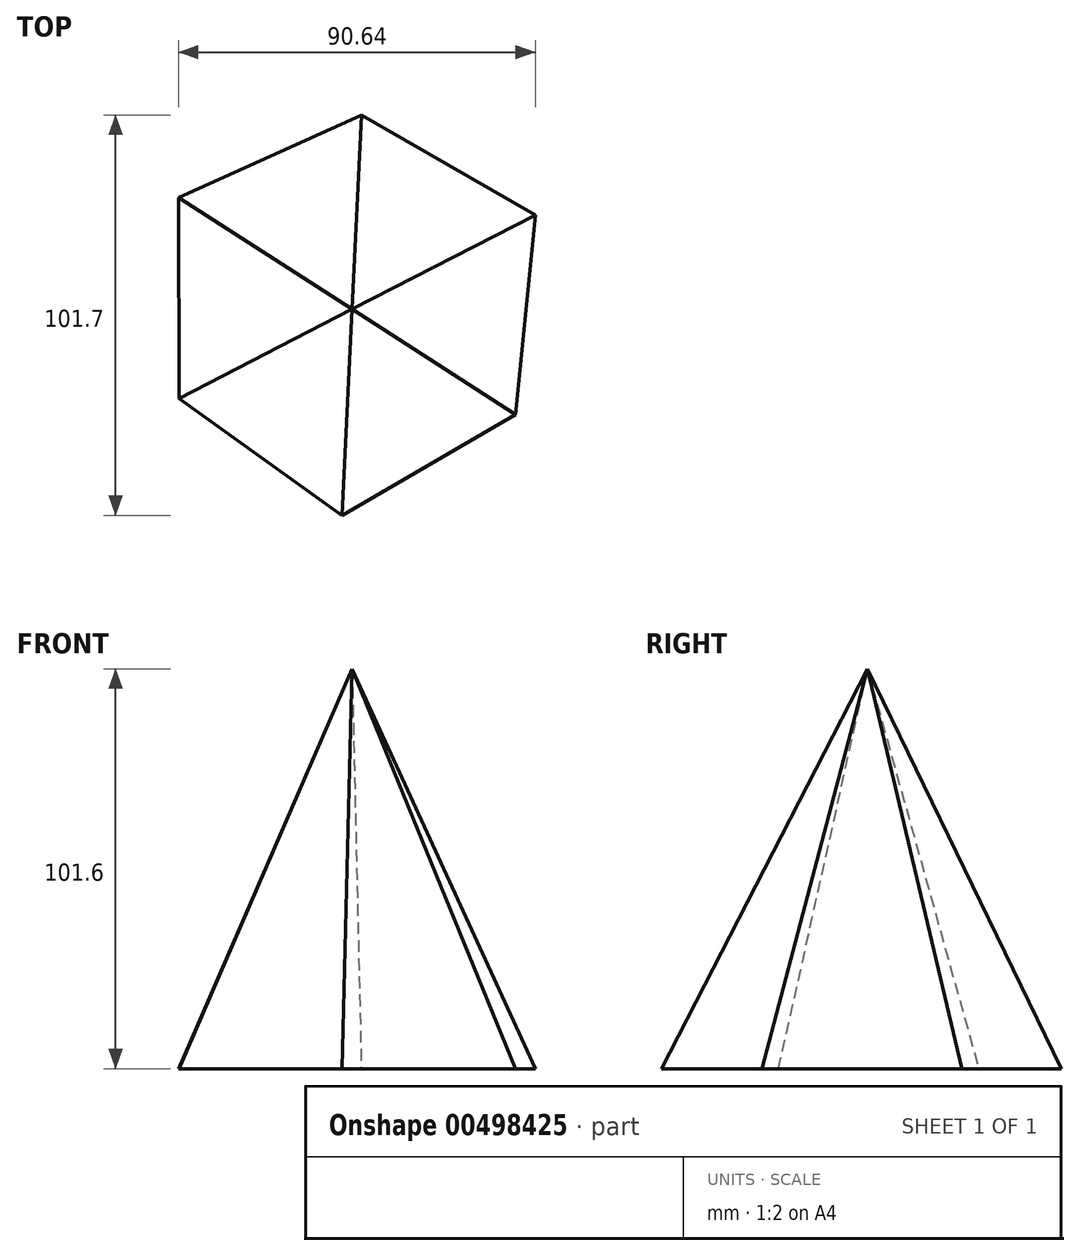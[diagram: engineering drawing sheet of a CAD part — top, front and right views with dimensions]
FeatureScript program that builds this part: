
annotation { "Feature Type Name" : "Feature", "Feature Type Description" : "" }
export const myFeature = defineFeature(function(context is Context, id is Id, definition is map)
    precondition{}
    {
        {
            var Q0;
            Q0=qCreatedBy(makeId("Top.planeOp"),FACE);
            var sketch = newSketch(context, id + "F0", { "sketchPlane" : qUnion([Q0])});
            skCircle(sketch, "E0.cCircle", {"center": v(0, 0) * mm, "radius": 87.99 * mm, "construction": true});
            skLineSegment(sketch, "E0.0", {"start": v(-44.2, 76.08) * mm, "end": v(87.99, 0.23) * mm});
            skLineSegment(sketch, "E0.1", {"start": v(87.99, 0.23) * mm, "end": v(-43.8, -76.32) * mm});
            skLineSegment(sketch, "E0.2", {"start": v(-43.8, -76.32) * mm, "end": v(-44.2, 76.08) * mm});
            skLineSegment(sketch, "E1.0", {"start": v(51.24, 71.53) * mm, "end": v(36.32, -80.14) * mm});
            skLineSegment(sketch, "E1.1", {"start": v(36.32, -80.14) * mm, "end": v(-87.57, 8.61) * mm});
            skLineSegment(sketch, "E1.2", {"start": v(-87.57, 8.61) * mm, "end": v(51.24, 71.53) * mm});
            skSolve(sketch);
        }
        {
            var Q0;
            Q0=qCreatedBy(makeId("Top.planeOp"),FACE);
            cPlane(context, id + "F1", {"entities" : qUnion([Q0]), "cplaneType" : CPlaneType.OFFSET, "offset" : 101.6 * mm, "width" : 152.4 * mm, "height" : 152.4 * mm});
        }
        {
            var Q0;
            Q0=qCreatedBy(id+"F1.planeOp",FACE);
            var sketch = newSketch(context, id + "F2", { "sketchPlane" : qUnion([Q0])});
            skPoint(sketch, "E2", {"position": v(0, 0) * mm});
            skSolve(sketch);
        }
        {
            var Q0;
            Q0=sQuery(id+"F2.wireOp",VERTEX,"E2");
            var Q1;
            {var subQ1=sQuery(id+"F0.wireOp",EDGE,"E0.0");var subQ8=sQuery(id+"F0.wireOp",EDGE,"E1.2");var subQ11=makeQuery(id+"F0.imprint","INTERSECT",VERTEX,{"derivedFrom":[subQ1,subQ8]});Q1=makeQuery(id+"F0.imprint","IMPRINT",FACE,{"disambiguationData":[TD([[makeQuery(id+"F0.imprint","IMPRINT",EDGE,{"disambiguationData":[TD([[subQ11,-1.0]])],"derivedFrom":subQ1}),-1.0]])]});}
            loft(context, id + "F3", {"sheetProfilesArray" : [{ "sheetProfileEntities" : qUnion([Q0]) }, { "sheetProfileEntities" : qUnion([Q1]) }]});
        }
    });
